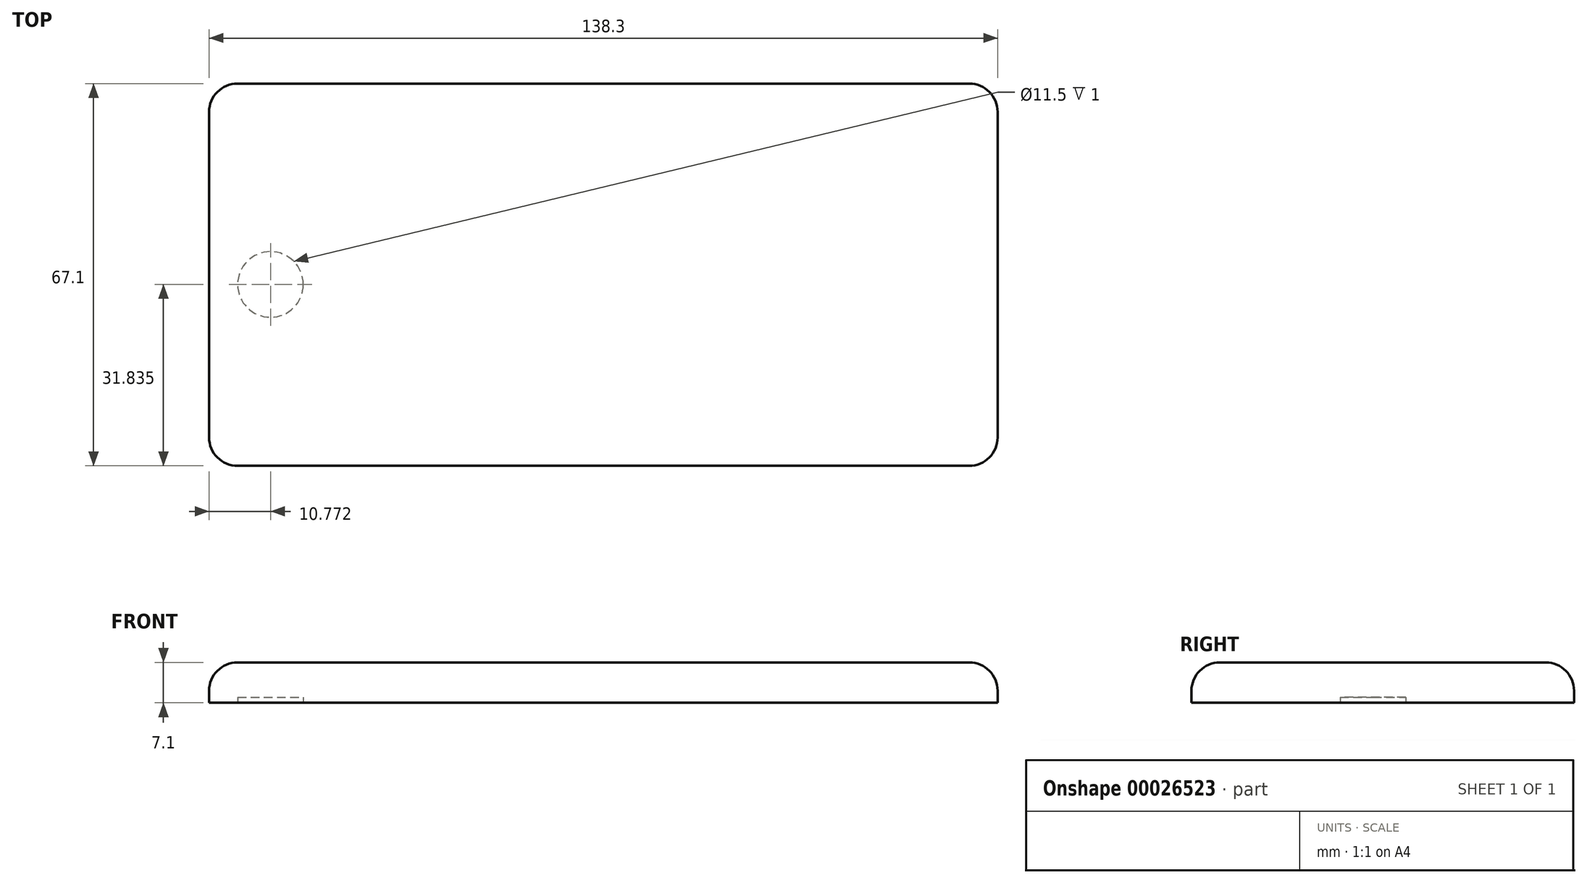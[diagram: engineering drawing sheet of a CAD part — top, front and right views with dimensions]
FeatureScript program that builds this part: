
annotation { "Feature Type Name" : "Feature", "Feature Type Description" : "" }
export const myFeature = defineFeature(function(context is Context, id is Id, definition is map)
    precondition{}
    {
        {
            var Q0;
            Q0=qCreatedBy(makeId("Top.planeOp"),FACE);
            var sketch = newSketch(context, id + "F0", { "sketchPlane" : qUnion([Q0])});
            skLineSegment(sketch, "E0.bottom", {"start": v(0, 0) * mm, "end": v(-138.3, 0) * mm});
            skLineSegment(sketch, "E0.top", {"start": v(0, 67.1) * mm, "end": v(-138.3, 67.1) * mm});
            skLineSegment(sketch, "E0.left", {"start": v(0, 0) * mm, "end": v(0, 67.1) * mm});
            skLineSegment(sketch, "E0.right", {"start": v(-138.3, 0) * mm, "end": v(-138.3, 67.1) * mm});
            skSolve(sketch);
        }
        {
            var Q0;
            Q0=makeQuery(id+"F0.imprint","IMPRINT",FACE,{"disambiguationData":[TD([[makeQuery(id+"F0.imprint","IMPRINT",EDGE,{"derivedFrom":sQuery(id+"F0.wireOp",EDGE,"E0.bottom")}),-1.0]])]});
            extrude(context, id + "F1", {"entities" : qUnion([Q0]), "depth" : 7.1 * mm});
        }
        {
            var Q0;
            Q0=makeQuery(id+"F1.opExtrude","SWEPT_EDGE",EDGE,{"disambiguationData":[OSD([sQuery(id+"F0.wireOp",EDGE,"E0.bottom"),sQuery(id+"F0.wireOp",EDGE,"E0.left")])]});
            var Q1;
            Q1=makeQuery(id+"F1.opExtrude","SWEPT_EDGE",EDGE,{"disambiguationData":[OSD([sQuery(id+"F0.wireOp",EDGE,"E0.bottom"),sQuery(id+"F0.wireOp",EDGE,"E0.right")])]});
            fillet(context, id + "F2", {"entities" : qUnion([Q0, Q1]), "radius" : 5 * mm, "tangentPropagation" : true, "allowEdgeOverflow" : false});
        }
        {
            var Q0;
            Q0=makeQuery(id+"F1.opExtrude","SWEPT_EDGE",EDGE,{"disambiguationData":[OSD([sQuery(id+"F0.wireOp",EDGE,"E0.top"),sQuery(id+"F0.wireOp",EDGE,"E0.right")])]});
            fillet(context, id + "F3", {"entities" : qUnion([Q0]), "radius" : 5 * mm, "tangentPropagation" : true, "allowEdgeOverflow" : false});
        }
        {
            var Q0;
            Q0=makeQuery(id+"F1.opExtrude","SWEPT_EDGE",EDGE,{"disambiguationData":[OSD([sQuery(id+"F0.wireOp",EDGE,"E0.top"),sQuery(id+"F0.wireOp",EDGE,"E0.left")])]});
            fillet(context, id + "F4", {"entities" : qUnion([Q0]), "radius" : 5 * mm, "tangentPropagation" : true, "allowEdgeOverflow" : false});
        }
        {
            var Q0;
            Q0=makeQuery(id+"F1.opExtrude","CAP_EDGE",EDGE,{"disambiguationData":[OSD([sQuery(id+"F0.wireOp",EDGE,"E0.top")])],"isStart":false});
            fillet(context, id + "F5", {"entities" : qUnion([Q0]), "radius" : 5 * mm, "tangentPropagation" : true, "allowEdgeOverflow" : false});
        }
        {
            var Q0;
            Q0=makeQuery(id+"F1.opExtrude","CAP_FACE",FACE,{"disambiguationData":[OSD([sQuery(id+"F0.wireOp",EDGE,"E0.bottom"),sQuery(id+"F0.wireOp",EDGE,"E0.top"),sQuery(id+"F0.wireOp",EDGE,"E0.left"),sQuery(id+"F0.wireOp",EDGE,"E0.right")])],"isStart":true});
            var sketch = newSketch(context, id + "F6", { "sketchPlane" : qUnion([Q0])});
            skCircle(sketch, "E1", {"center": v(-127.53, -31.84) * mm, "radius": 5.75 * mm});
            skSolve(sketch);
        }
        {
            var Q0;
            Q0 = qSketchRegion(id + "F6", true);
            extrude(context, id + "F7", {"entities" : qUnion([Q0]), "operationType" : NewBodyOperationType.REMOVE, "oppositeDirection" : true, "depth" : 1 * mm});
        }
    });
